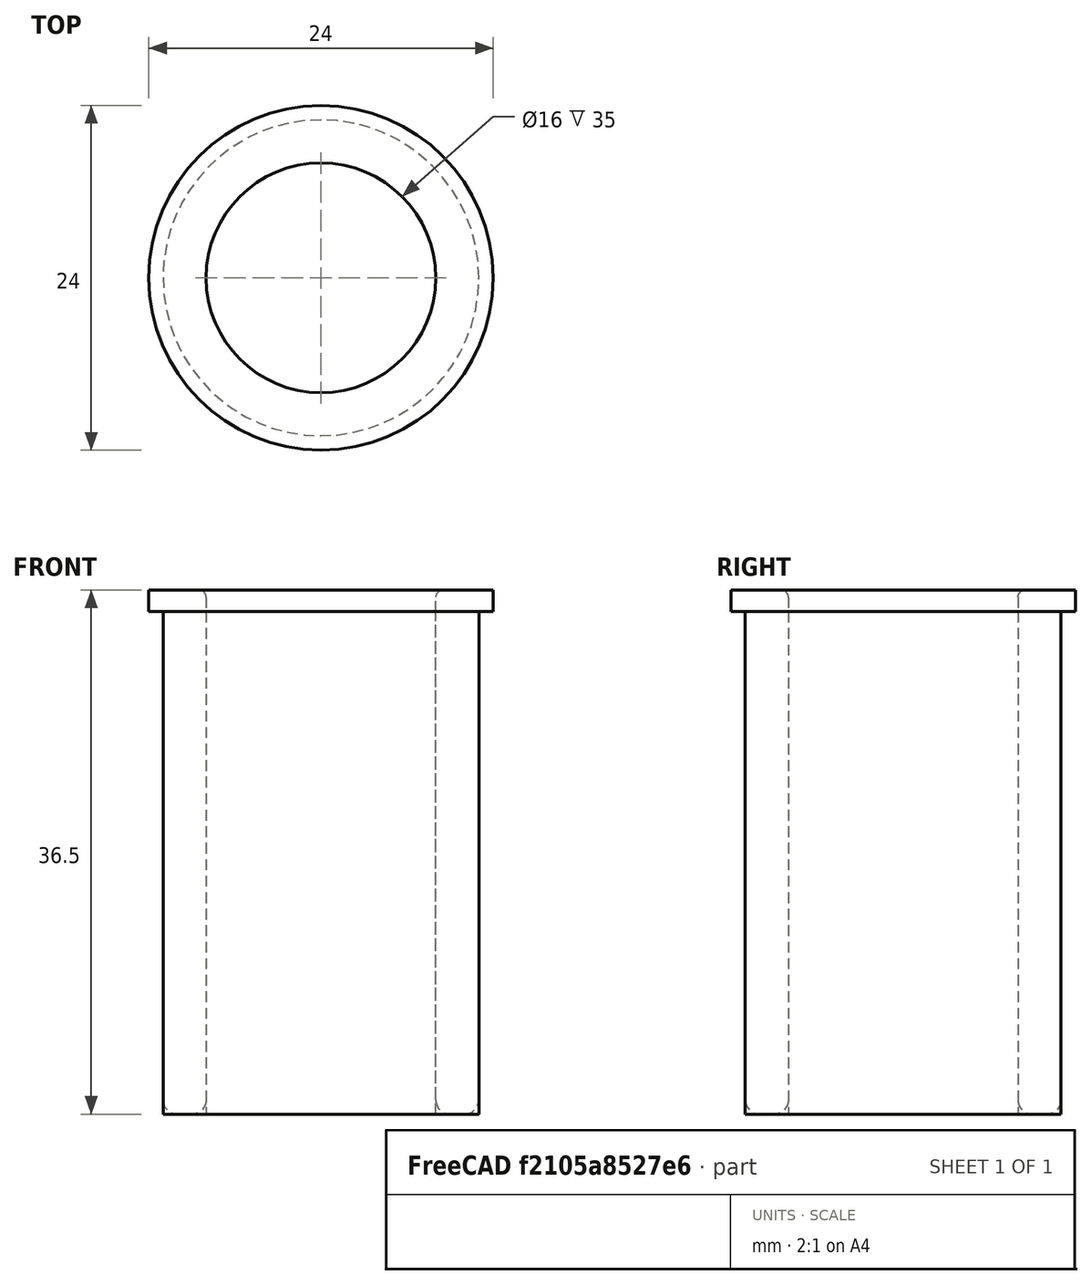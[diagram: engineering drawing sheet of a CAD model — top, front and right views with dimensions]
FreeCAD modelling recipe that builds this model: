
FCSTD DOCUMENT  (FreeCAD 0.16R)
Label: StriderSpacer
License: All rights reserved
LicenseURL: http://en.wikipedia.org/wiki/All_rights_reserved
objects: Sketcher::SketchObject×2, PartDesign::Pad×2, PartDesign::Fillet×2, Mesh::Feature×1
note: 8 computed .brp shape members not serialized (recipe doc carries the construction recipe); baked Part::Feature solids carry a one-line shape summary decoded from their .brp

FEATURE [Sketcher::SketchObject] Sketch
  sketch-geometry (2):
    g0: Circle CenterX=0 CenterY=0 CenterZ=0 NormalX=0 NormalY=0 NormalZ=1 Radius=11
    g1: Circle CenterX=0 CenterY=0 CenterZ=0 NormalX=0 NormalY=0 NormalZ=1 Radius=8
  constraints (4):
    c: Coincident(g-1,g0)
    c: Radius(g0) = 11
    c: Coincident(g1,g-1)
    c: Radius(g1) = 8
FEATURE [PartDesign::Pad] Pad
  Length = 35
  Length2 = 100
  Sketch = -> Sketch
  Type = 0
FEATURE [Sketcher::SketchObject] Sketch001
  Placement = pos=(0,0,35) rot=(0,0,1;0rad)
  Support = -> Pad [Face4]
  sketch-geometry (2):
    g0: Circle CenterX=0 CenterY=0 CenterZ=0 NormalX=0 NormalY=0 NormalZ=1 Radius=12
    g1: Circle CenterX=0 CenterY=0 CenterZ=0 NormalX=0 NormalY=0 NormalZ=1 Radius=8
  constraints (4):
    c: Coincident(g0,g-1)
    c: Radius(g0) = 12
    c: Coincident(g1,g-1)
    c: Radius(g1) = 8
FEATURE [PartDesign::Pad] Pad001
  Length = 1.5
  Length2 = 100
  Sketch = -> Sketch001
  Type = 0
FEATURE [PartDesign::Fillet] Fillet
  Base = -> Pad001 [Edge1,Edge2]
  Radius = 1
FEATURE [PartDesign::Fillet] Fillet001
  Base = -> Fillet [Edge13]
  Radius = 0.5
FEATURE [Mesh::Feature] Mesh  label="Fillet001 (Meshed)"
